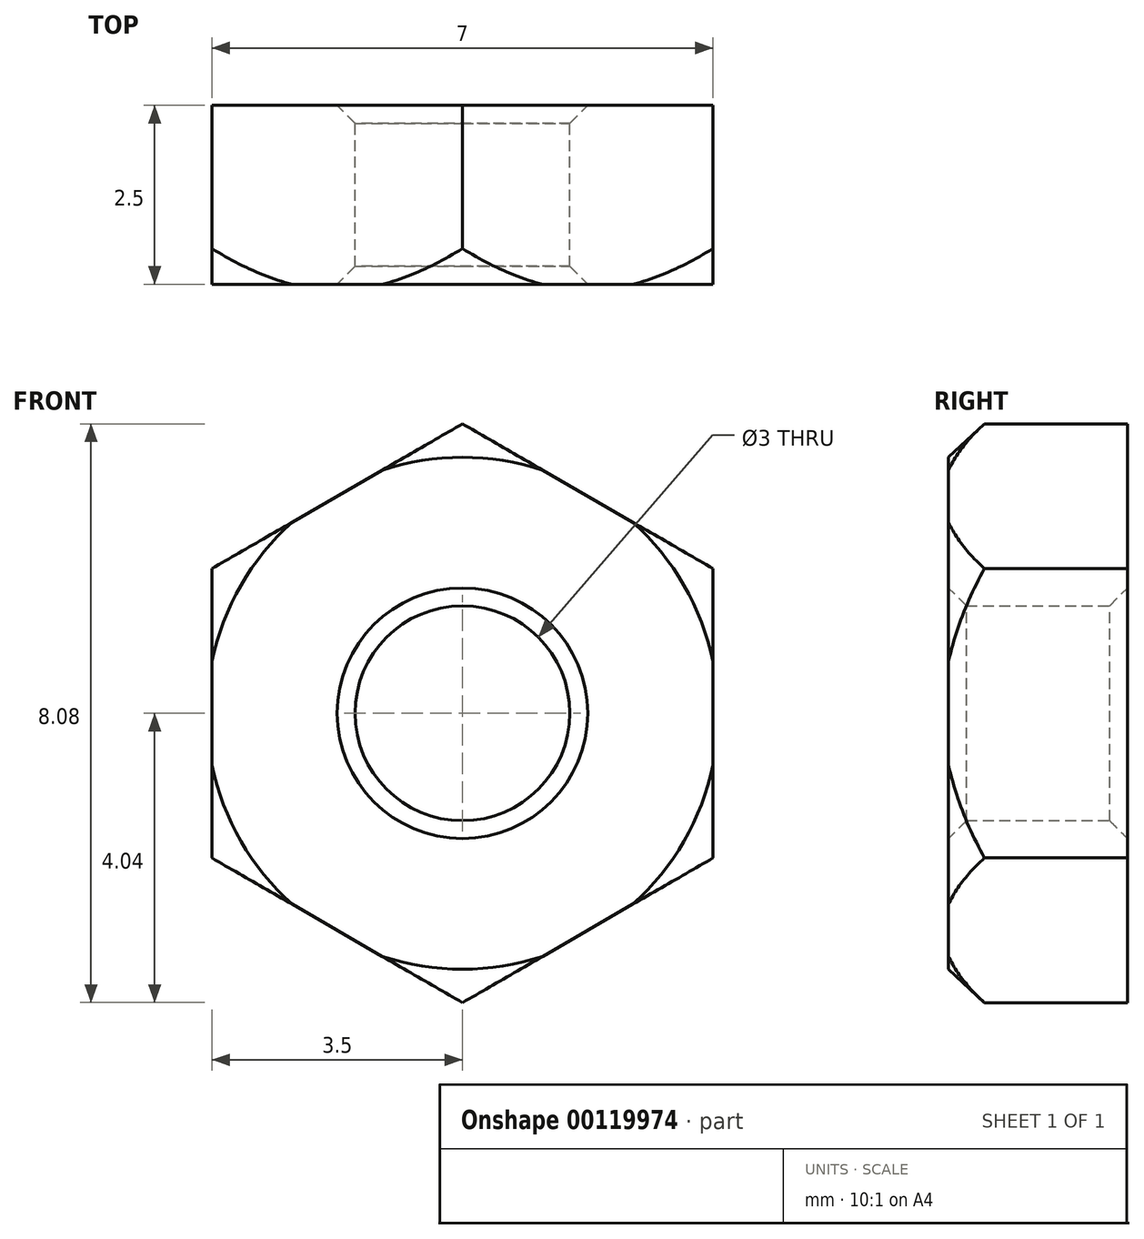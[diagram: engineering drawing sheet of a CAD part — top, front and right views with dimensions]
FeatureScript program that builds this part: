
annotation { "Feature Type Name" : "Feature", "Feature Type Description" : "" }
export const myFeature = defineFeature(function(context is Context, id is Id, definition is map)
    precondition{}
    {
        {
            var Q0;
            Q0=qCreatedBy(makeId("Front.planeOp"),FACE);
            var sketch = newSketch(context, id + "F0", { "sketchPlane" : qUnion([Q0])});
            skCircle(sketch, "E0.cCircle", {"center": v(0, 0) * mm, "radius": 3.5 * mm, "construction": true});
            skLineSegment(sketch, "E0.0", {"start": v(0, 4.04) * mm, "end": v(3.5, 2.02) * mm});
            skLineSegment(sketch, "E0.1", {"start": v(3.5, 2.02) * mm, "end": v(3.5, -2.02) * mm});
            skLineSegment(sketch, "E0.2", {"start": v(3.5, -2.02) * mm, "end": v(0, -4.04) * mm});
            skLineSegment(sketch, "E0.3", {"start": v(0, -4.04) * mm, "end": v(-3.5, -2.02) * mm});
            skLineSegment(sketch, "E0.4", {"start": v(-3.5, -2.02) * mm, "end": v(-3.5, 2.02) * mm});
            skLineSegment(sketch, "E0.5", {"start": v(-3.5, 2.02) * mm, "end": v(0, 4.04) * mm});
            skPoint(sketch, "E0.0.midPoint", {"position": v(1.75, 3.03) * mm});
            skCircle(sketch, "E1", {"center": v(0, 0) * mm, "radius": 1.5 * mm});
            skSolve(sketch);
        }
        {
            var Q0;
            Q0 = qSketchRegion(id + "F0", true);
            extrude(context, id + "F1", {"entities" : qUnion([Q0]), "endBound" : BoundingType.SYMMETRIC, "depth" : 2.5 * mm});
        }
        {
            var Q0;
            Q0=qCreatedBy(makeId("Right.planeOp"),FACE);
            var sketch = newSketch(context, id + "F2", { "sketchPlane" : qUnion([Q0])});
            skLineSegment(sketch, "E2", {"start": v(-1.25, 4.04) * mm, "end": v(-0.75, 4.04) * mm});
            skLineSegment(sketch, "E3", {"start": v(-0.75, 4.04) * mm, "end": v(-1.25, 3.57) * mm});
            skLineSegment(sketch, "E4", {"start": v(-1.25, 3.57) * mm, "end": v(-1.25, 4.04) * mm});
            skSolve(sketch);
        }
        {
            var Q0;
            Q0 = qSketchRegion(id + "F2", true);
            var Q1;
            Q1=makeQuery(id+"F1.opExtrude","SWEPT_FACE",FACE,{"disambiguationData":[OSD([sQuery(id+"F0.wireOp",EDGE,"E1")])]});
            revolve(context, id + "F3", {"operationType" : NewBodyOperationType.REMOVE, "entities" : qUnion([Q0]), "axis" : qUnion([Q1]), "revolveType" : RevolveType.FULL, "oppositeDirection" : true});
        }
        {
            var Q0;
            Q0=makeQuery(id+"F1.opExtrude","SWEPT_FACE",FACE,{"disambiguationData":[OSD([sQuery(id+"F0.wireOp",EDGE,"E1")])]});
            chamfer(context, id + "F4", {"entities" : qUnion([Q0]), "width" : .25 * mm, "tangentPropagation" : true});
        }
    });
